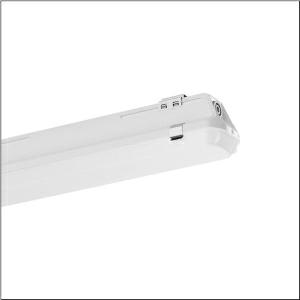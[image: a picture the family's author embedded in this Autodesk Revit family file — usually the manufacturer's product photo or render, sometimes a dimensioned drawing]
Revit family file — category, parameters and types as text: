
# Revit family: monsun_r__11_parking_51fg207p440h_0f51
name_source: partatom
category: Lighting Fixtures
units: mm (PartAtom-declared; Revit-internal decimal feet)

## family parameters
Cut with Voids When Loaded = No
Host = Face
Light Source = No
Part Type = Normal
Room Calculation Point = No
Round Connector Dimension = Use Diameter
Shared = No

## types (1)
- Monsun® 11 parking (1 x LED, 4820 lm, 29.2 W, 4000K)
    Apparent Load = 29 VA
    CIE Flux Codes = 45 75 93 94 100
    Color Rendering = 80
    Color Temperature = 4000K
    Default Elevation = 1800 mm
    Description = Monsun® 11 parking, damp-proof luminaire, chain hanger, primary optical cover: enclosure, of PC, light emission: direct distribution, primary light characteristic: symmetric, installation type: suspended mounting, surface-mounted, horizontal mounting, vertical mounting, LED, rated luminous flux: 4.820lm, luminous efficacy: 165lm/W, light colour: 840, colour temperature: 4000K, control gear: ECG, with terminal, 3-pole, max. 2.5mm², mains connection: 220..240V, AC, 50/60Hz, rated input power: 29W, housing, of glass-fibre reinforced polyester, uncoated, bright grey, incl. chain hanger, length: 1.590mm, width: 90mm, height: 88mm, clip for enclosure, of stainless steel (V2A), ceiling mounting element, of stainless steel (V2A), chain hanger, of stainless steel (V2A), protection rating (complete): IP66, insulation class (complete): insulation class I (protective earthing), certification: CE, ENEC, VDE, UKCA, protection symbol: D, impact resistance: IK08, permissible operating ambient temperature: -35..+40°C, standard: EN 50419, EN 60598-2-1, no direct snow, no direct sun, no direct rain, for indoor or canopied outdoor use, corresponds to IFS (International Featured Standards) requirements for safety and quality in the food industry, contact your sales advisor before using the luminaires in applications with unclear chemical exposure, large temperature fluctuations or condensation-forming humidity, LABS conformity tested according to VDMA 24364:2018-05, packaging unit: 1 piece
    Height = 89 mm
    Lamp = 1 x LED
    Lamp Light Flux = 4820 lm
    Lamp Power = 29.2 W
    Lamp count = 1
    Length = 1590 mm
    Luminous efficacy = 165 lm/W
    Manufacturer = Siteco
    ModVariant = No
    Model = 51FG207P440H
    Mounting Place = Ceiling
    Mounting Type = Surface mounted
    Number of Poles = 1
    OnlyDefault = Yes
    Power Factor = 1
    Product Name = Monsun® 11 parking
    Product group = damp-proof luminaire
    ProductGroupID = 301
    Protection Class = Protection class I
    Protection Degree = IP 66
    RLX_Detail_Level = 1
    RLX_Emergency_Light_Flux = 0 lm
    RLX_Emergency_Type = 0
    RLX_Emergency_Type_DB = No
    RlxData = <blob elided: 88565 chars, md5=d631ae76>
    Socket = socket
    Standby Power = 0 W
    System Light Flux = 4820 lm
    System Power = 29 W
    Type Comments = Product without accessories
    Type Image = l_1004748.jpg
    URL = http://relux.com
    VarID = ---
    Voltage = 0 V
    Weight = 0.00 kg
    Width = 90 mm

## geometry (parser evidence)
native form markers: Blend x4, Sweep x13
no freeform markers — native parametric forms only
